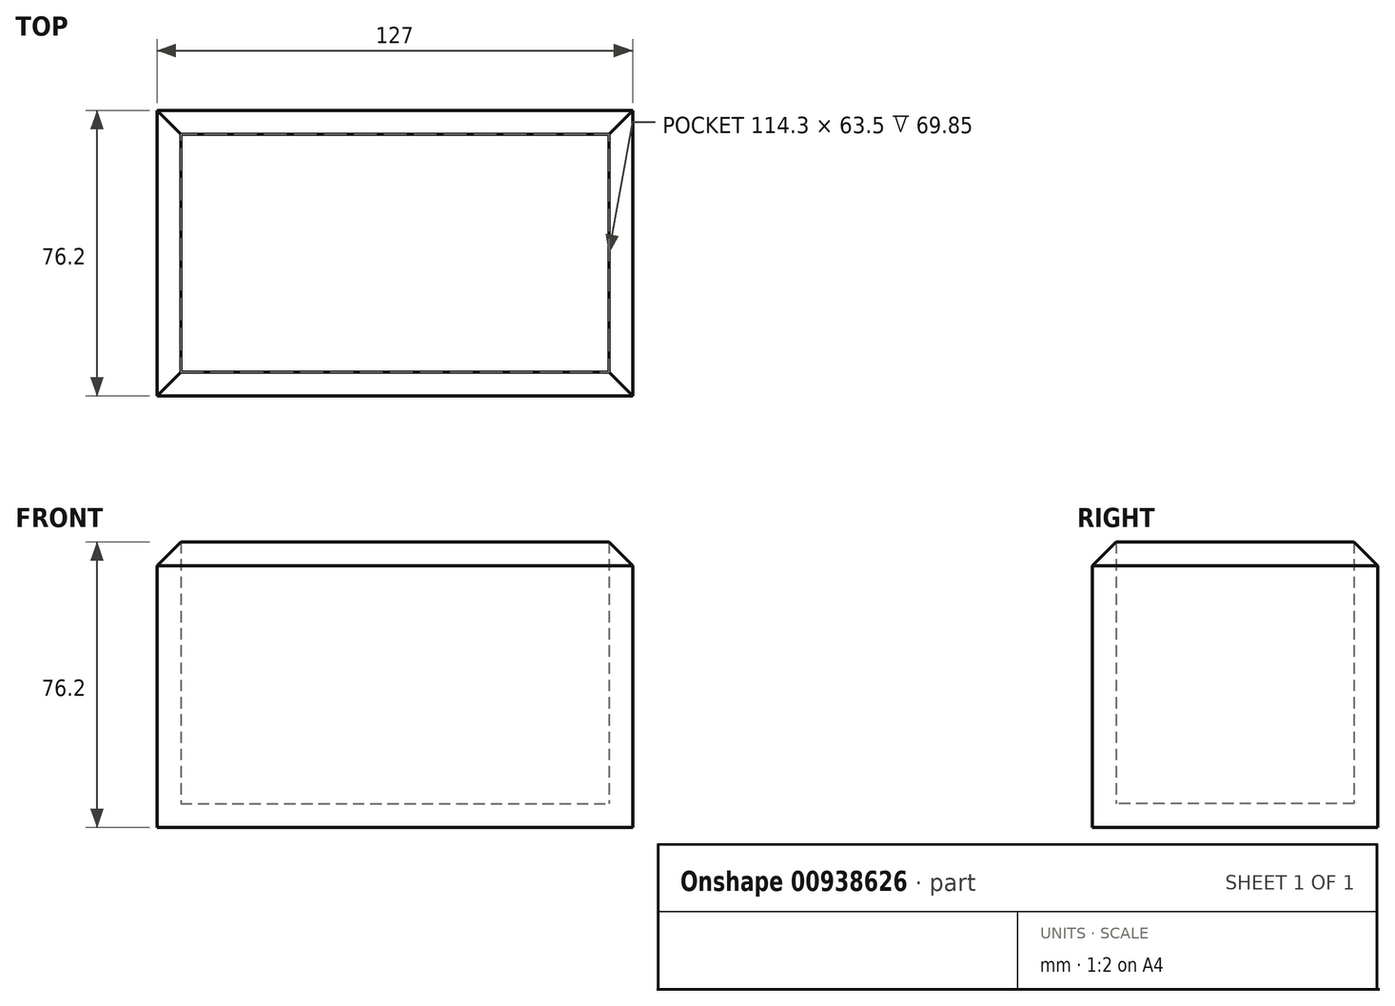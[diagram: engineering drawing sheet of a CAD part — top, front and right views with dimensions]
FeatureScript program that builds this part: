
annotation { "Feature Type Name" : "Feature", "Feature Type Description" : "" }
export const myFeature = defineFeature(function(context is Context, id is Id, definition is map)
    precondition{}
    {
        {
            var Q0;
            Q0=qCreatedBy(makeId("Top.planeOp"),FACE);
            var sketch = newSketch(context, id + "F0", { "sketchPlane" : qUnion([Q0])});
            skLineSegment(sketch, "E0.bottom", {"start": v(-62.1, 26.77) * mm, "end": v(64.9, 26.77) * mm});
            skLineSegment(sketch, "E0.top", {"start": v(-62.1, -49.43) * mm, "end": v(64.9, -49.43) * mm});
            skLineSegment(sketch, "E0.left", {"start": v(-62.1, 26.77) * mm, "end": v(-62.1, -49.43) * mm});
            skLineSegment(sketch, "E0.right", {"start": v(64.9, 26.77) * mm, "end": v(64.9, -49.43) * mm});
            skSolve(sketch);
        }
        {
            var Q0;
            Q0=makeQuery(id+"F0.imprint","IMPRINT",FACE,{"disambiguationData":[TD([[makeQuery(id+"F0.imprint","IMPRINT",EDGE,{"derivedFrom":sQuery(id+"F0.wireOp",EDGE,"E0.bottom")}),-1.0]])]});
            extrude(context, id + "F1", {"entities" : qUnion([Q0]), "depth" : 76.2 * mm, "offsetDistance" : 25.4 * mm});
        }
        {
            var Q0;
            Q0=makeQuery(id+"F1.opExtrude","CAP_FACE",FACE,{"disambiguationData":[OSD([sQuery(id+"F0.wireOp",EDGE,"E0.bottom"),sQuery(id+"F0.wireOp",EDGE,"E0.top"),sQuery(id+"F0.wireOp",EDGE,"E0.left"),sQuery(id+"F0.wireOp",EDGE,"E0.right")])],"isStart":false});
            shell(context, id + "F2", {"entities" : qUnion([Q0]), "thickness" : 6.35 * mm});
        }
        {
            var Q0;
            Q0=makeQuery(id+"F1.opExtrude","CAP_EDGE",EDGE,{"disambiguationData":[OSD([sQuery(id+"F0.wireOp",EDGE,"E0.top")])],"isStart":false});
            var Q1;
            Q1=makeQuery(id+"F1.opExtrude","CAP_EDGE",EDGE,{"disambiguationData":[OSD([sQuery(id+"F0.wireOp",EDGE,"E0.bottom")])],"isStart":false});
            var Q2;
            Q2=makeQuery(id+"F1.opExtrude","CAP_EDGE",EDGE,{"disambiguationData":[OSD([sQuery(id+"F0.wireOp",EDGE,"E0.right")])],"isStart":false});
            var Q3;
            Q3=makeQuery(id+"F1.opExtrude","CAP_EDGE",EDGE,{"disambiguationData":[OSD([sQuery(id+"F0.wireOp",EDGE,"E0.left")])],"isStart":false});
            chamfer(context, id + "F3", {"entities" : qUnion([Q0, Q1, Q2, Q3]), "width" : 6.35 * mm, "tangentPropagation" : true});
        }
    });
